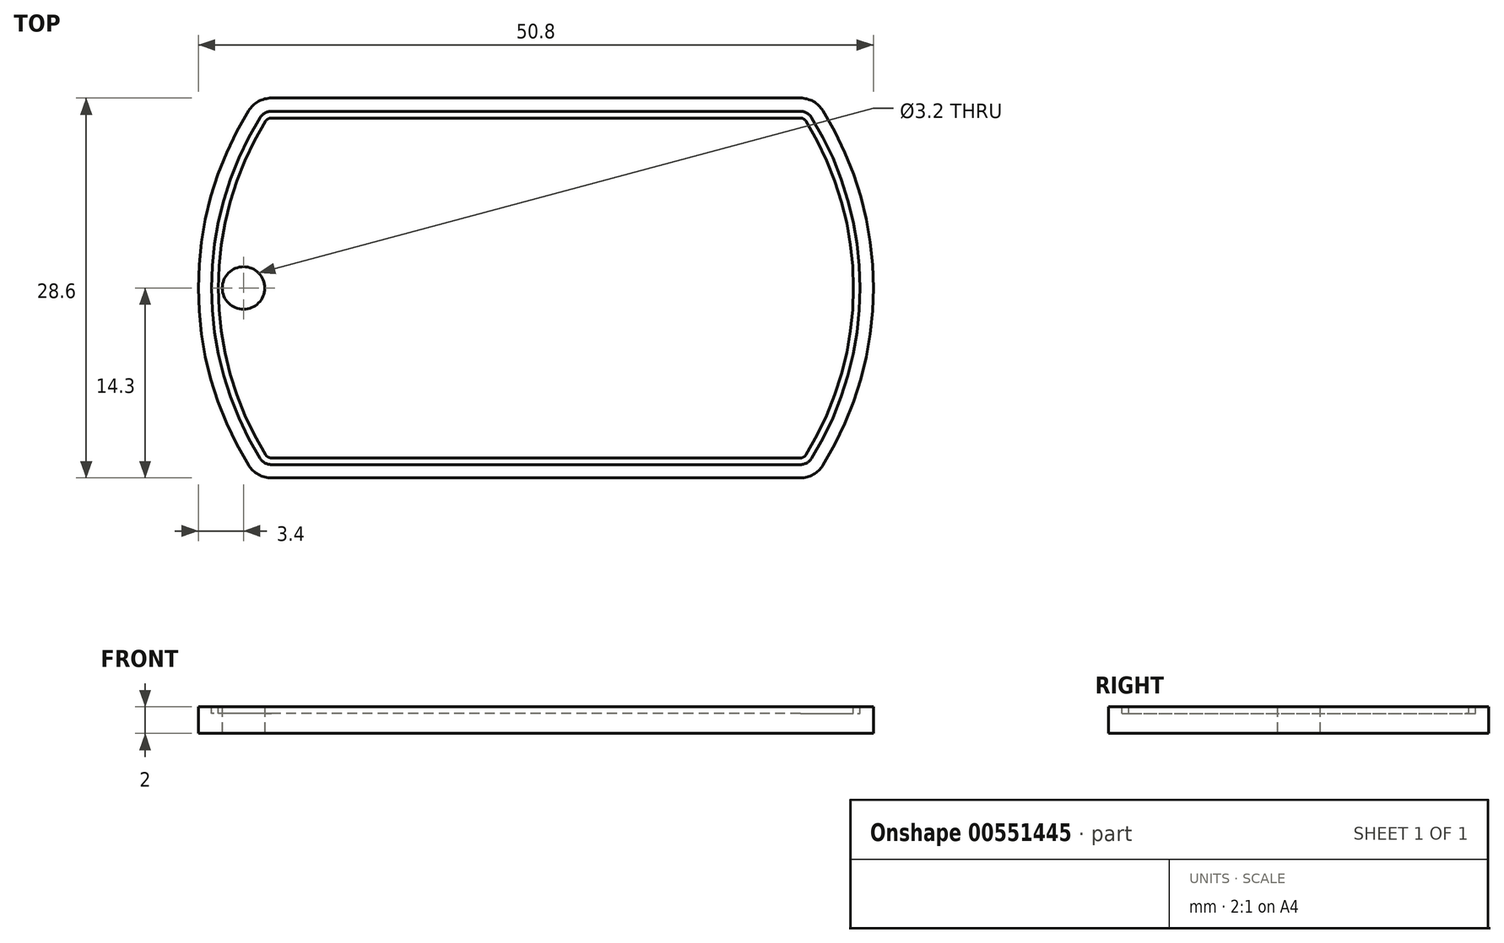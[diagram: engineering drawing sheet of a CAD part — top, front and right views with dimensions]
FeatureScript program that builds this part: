
annotation { "Feature Type Name" : "Feature", "Feature Type Description" : "" }
export const myFeature = defineFeature(function(context is Context, id is Id, definition is map)
    precondition{}
    {
        {
            var Q0;
            Q0=qCreatedBy(makeId("Top.planeOp"),FACE);
            var sketch = newSketch(context, id + "F0", { "sketchPlane" : qUnion([Q0])});
            skLineSegment(sketch, "E0.bottom", {"start": v(19.9, -14.3) * mm, "end": v(-19.9, -14.3) * mm});
            skLineSegment(sketch, "E0.top", {"start": v(19.9, 14.3) * mm, "end": v(-19.9, 14.3) * mm});
            skPoint(sketch, "E0.middle", {"position": v(0, 0) * mm});
            skArc(sketch, "E1", {"start": v(-21.6, 13.35) * mm, "mid": v(-25.4, 0) * mm, "end": v(-21.6, -13.35) * mm});
            skArc(sketch, "E2.trimOffspring", {"start": v(21.6, -13.35) * mm, "mid": v(25.4, 0) * mm, "end": v(21.6, 13.35) * mm});
            skPoint(sketch, "E3.orphan", {"position": v(-25.4, -14.3) * mm});
            skPoint(sketch, "E4.orphan", {"position": v(25.4, -14.3) * mm});
            skPoint(sketch, "E5.orphan", {"position": v(25.4, 14.3) * mm});
            skPoint(sketch, "E6.orphan", {"position": v(-25.4, 14.3) * mm});
            skCircle(sketch, "E7", {"center": v(-22, 0) * mm, "radius": 1.6 * mm});
            skPoint(sketch, "E8.visualSharp", {"position": v(21, 14.3) * mm});
            skArc(sketch, "E8.filletArc", {"start": v(21.6, 13.35) * mm, "mid": v(20.88, 14.05) * mm, "end": v(19.9, 14.3) * mm});
            skPoint(sketch, "E9.visualSharp", {"position": v(21, -14.3) * mm});
            skArc(sketch, "E9.filletArc", {"start": v(19.9, -14.3) * mm, "mid": v(20.88, -14.05) * mm, "end": v(21.6, -13.35) * mm});
            skPoint(sketch, "E10.visualSharp", {"position": v(-21, -14.3) * mm});
            skArc(sketch, "E10.filletArc", {"start": v(-21.6, -13.35) * mm, "mid": v(-20.88, -14.05) * mm, "end": v(-19.9, -14.3) * mm});
            skPoint(sketch, "E11.visualSharp", {"position": v(-21, 14.3) * mm});
            skArc(sketch, "E11.filletArc", {"start": v(-19.9, 14.3) * mm, "mid": v(-20.88, 14.05) * mm, "end": v(-21.6, 13.35) * mm});
            skSolve(sketch);
        }
        {
            var Q0;
            Q0=makeQuery(id+"F0.imprint","IMPRINT",FACE,{"disambiguationData":[TD([[makeQuery(id+"F0.imprint","IMPRINT",EDGE,{"derivedFrom":sQuery(id+"F0.wireOp",EDGE,"E0.bottom")}),-1.0]])]});
            extrude(context, id + "F1", {"entities" : qUnion([Q0]), "depth" : 2 * mm});
        }
        {
            var Q0;
            {var subQ0=sQuery(id+"F0.wireOp",EDGE,"E2.trimOffspring");var subQ1=sQuery(id+"F0.wireOp",EDGE,"E1");var subQ2=sQuery(id+"F0.wireOp",EDGE,"E10.filletArc");var subQ3=sQuery(id+"F0.wireOp",EDGE,"E9.filletArc");var subQ4=sQuery(id+"F0.wireOp",EDGE,"E8.filletArc");var subQ5=sQuery(id+"F0.wireOp",EDGE,"E7");var subQ6=sQuery(id+"F0.wireOp",EDGE,"E0.top");var subQ7=sQuery(id+"F0.wireOp",EDGE,"E0.bottom");var subQ8=sQuery(id+"F0.wireOp",EDGE,"E11.filletArc");Q0=makeQuery(id+"F1TJ1Icrn0PA5is_1.boolean.opBoolean","SPLIT",FACE,{"disambiguationData":[TD([makeQuery(id+"F1.opExtrude","SWEPT_FACE",FACE,{"disambiguationData":[OSD([subQ7])]})])],"derivedFrom":makeQuery(id+"F1.opExtrude","CAP_FACE",FACE,{"disambiguationData":[OSD([subQ7,subQ6,subQ1,subQ0,subQ5,subQ4,subQ3,subQ2,subQ8])],"isStart":false})});}
            var sketch = newSketch(context, id + "F2", { "sketchPlane" : qUnion([Q0])});
            skArc(sketch, "E12.0.0", {"start": v(21.6, 13.35) * mm, "mid": v(20.88, 14.05) * mm, "end": v(19.9, 14.3) * mm});
            skLineSegment(sketch, "E12.0.1", {"start": v(19.9, 14.3) * mm, "end": v(-19.9, 14.3) * mm});
            skArc(sketch, "E12.0.2", {"start": v(-19.9, 14.3) * mm, "mid": v(-20.88, 14.05) * mm, "end": v(-21.6, 13.35) * mm});
            skArc(sketch, "E12.0.3", {"start": v(-21.6, 13.35) * mm, "mid": v(-25.4, 0) * mm, "end": v(-21.6, -13.35) * mm});
            skArc(sketch, "E12.0.4", {"start": v(-21.6, -13.35) * mm, "mid": v(-20.88, -14.05) * mm, "end": v(-19.9, -14.3) * mm});
            skLineSegment(sketch, "E12.0.5", {"start": v(-19.9, -14.3) * mm, "end": v(19.9, -14.3) * mm});
            skArc(sketch, "E12.0.6", {"start": v(19.9, -14.3) * mm, "mid": v(20.88, -14.05) * mm, "end": v(21.6, -13.35) * mm});
            skArc(sketch, "E12.0.7", {"start": v(21.6, -13.35) * mm, "mid": v(25.4, 0) * mm, "end": v(21.6, 13.35) * mm});
            skArc(sketch, "E13.0", {"start": v(20.33, -12.56) * mm, "mid": v(23.9, 0) * mm, "end": v(20.33, 12.56) * mm});
            skArc(sketch, "E13.1", {"start": v(19.9, -12.8) * mm, "mid": v(20.15, -12.74) * mm, "end": v(20.33, -12.56) * mm});
            skArc(sketch, "E13.2", {"start": v(20.33, 12.56) * mm, "mid": v(20.15, 12.74) * mm, "end": v(19.9, 12.8) * mm});
            skLineSegment(sketch, "E13.3", {"start": v(-19.9, -12.8) * mm, "end": v(19.9, -12.8) * mm});
            skLineSegment(sketch, "E13.4", {"start": v(19.9, 12.8) * mm, "end": v(-19.9, 12.8) * mm});
            skArc(sketch, "E13.5", {"start": v(-19.9, 12.8) * mm, "mid": v(-20.15, 12.74) * mm, "end": v(-20.33, 12.56) * mm});
            skArc(sketch, "E13.6", {"start": v(-20.33, 12.56) * mm, "mid": v(-23.9, 0) * mm, "end": v(-20.33, -12.56) * mm});
            skArc(sketch, "E13.7", {"start": v(-20.33, -12.56) * mm, "mid": v(-20.15, -12.74) * mm, "end": v(-19.9, -12.8) * mm});
            skArc(sketch, "E14.0", {"start": v(20.76, -12.83) * mm, "mid": v(24.4, 0) * mm, "end": v(20.76, 12.83) * mm});
            skArc(sketch, "E14.1", {"start": v(19.9, -13.3) * mm, "mid": v(20.4, -13.17) * mm, "end": v(20.76, -12.83) * mm});
            skArc(sketch, "E14.2", {"start": v(20.76, 12.83) * mm, "mid": v(20.4, 13.17) * mm, "end": v(19.9, 13.3) * mm});
            skLineSegment(sketch, "E14.3", {"start": v(-19.9, -13.3) * mm, "end": v(19.9, -13.3) * mm});
            skLineSegment(sketch, "E14.4", {"start": v(19.9, 13.3) * mm, "end": v(-19.9, 13.3) * mm});
            skArc(sketch, "E14.5", {"start": v(-19.9, 13.3) * mm, "mid": v(-20.4, 13.17) * mm, "end": v(-20.76, 12.83) * mm});
            skArc(sketch, "E14.6", {"start": v(-20.76, 12.83) * mm, "mid": v(-24.4, 0) * mm, "end": v(-20.76, -12.83) * mm});
            skArc(sketch, "E14.7", {"start": v(-20.76, -12.83) * mm, "mid": v(-20.4, -13.17) * mm, "end": v(-19.9, -13.3) * mm});
            skSolve(sketch);
        }
        {
            var Q0;
            Q0=makeQuery(id+"F2.imprint","IMPRINT",FACE,{"disambiguationData":[TD([[makeQuery(id+"F2.imprint","IMPRINT",EDGE,{"derivedFrom":sQuery(id+"F2.wireOp",EDGE,"E13.0")}),-1.0]])]});
            extrude(context, id + "F3", {"entities" : qUnion([Q0]), "operationType" : NewBodyOperationType.REMOVE, "oppositeDirection" : true, "depth" : .5 * mm});
        }
    });
